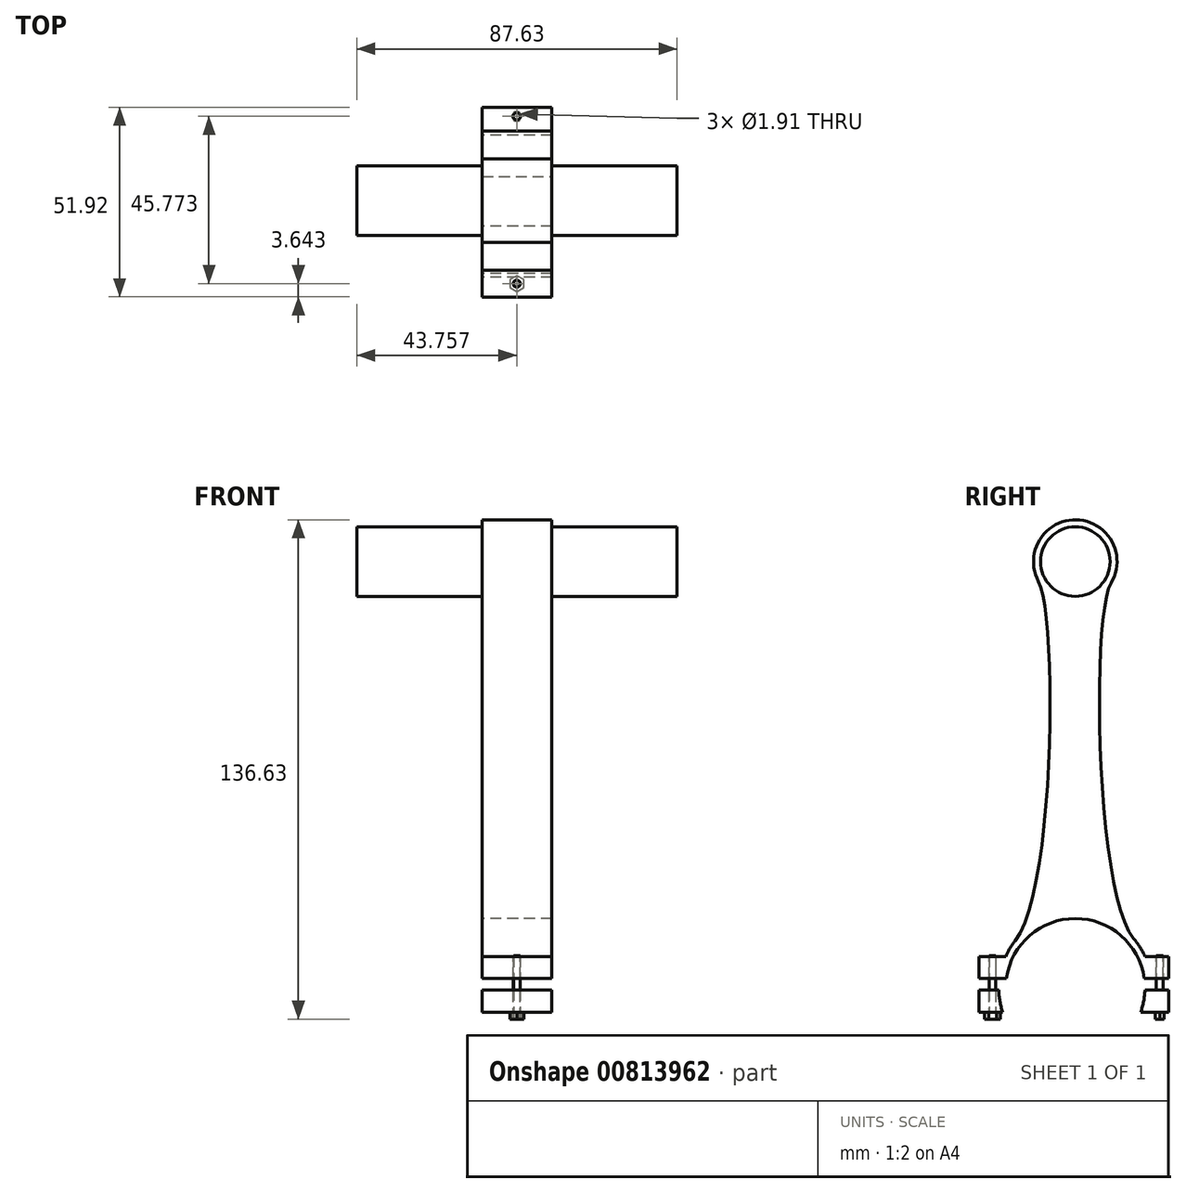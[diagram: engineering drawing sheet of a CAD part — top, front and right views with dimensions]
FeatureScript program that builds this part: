
annotation { "Feature Type Name" : "Feature", "Feature Type Description" : "" }
export const myFeature = defineFeature(function(context is Context, id is Id, definition is map)
    precondition{}
    {
        {
            var Q0;
            Q0=qCreatedBy(makeId("Right.planeOp"),FACE);
            var sketch = newSketch(context, id + "F0", { "sketchPlane" : qUnion([Q0])});
            skArc(sketch, "E0", {"start": v(-29.36, -1.03) * mm, "mid": v(-15.4, -14.68) * mm, "end": v(-1.43, -1.03) * mm});
            skCircle(sketch, "E1", {"center": v(-15.4, 77.12) * mm, "radius": 7.62 * mm});
            skFitSpline(sketch, "E2", {"points": [v(-22.11, 73.5) * mm, v(-26.4, 7.9) * mm], "startDerivative": vector(10.11, -18.68) * mm, "endDerivative": vector(-22.39, -28.64) * mm});
            skFitSpline(sketch, "E3", {"points": [v(-8.9, 73.18) * mm, v(-4.77, 8.36) * mm], "startDerivative": vector(-10.82, -17.88) * mm, "endDerivative": vector(20.78, -24.37) * mm});
            skCircle(sketch, "E4", {"center": v(-15.4, 77.12) * mm, "radius": 6.35 * mm});
            skArc(sketch, "E5", {"start": v(-28.1, -1.03) * mm, "mid": v(-15.4, -13.4) * mm, "end": v(-2.7, -1.03) * mm});
            skLineSegment(sketch, "E6", {"start": v(-29.35, 0) * mm, "end": v(-1.45, 0) * mm});
            skLineSegment(sketch, "E7.bottom", {"start": v(-32.95, 5.08) * mm, "end": v(1.67, 5.08) * mm});
            skLineSegment(sketch, "E7.top", {"start": v(-32.95, 0) * mm, "end": v(1.67, 0) * mm});
            skLineSegment(sketch, "E7.left", {"start": v(-32.95, 5.08) * mm, "end": v(-32.95, 1.1) * mm});
            skLineSegment(sketch, "E7.right", {"start": v(1.67, 5.08) * mm, "end": v(1.67, 1.1) * mm});
            skLineSegment(sketch, "E8.top", {"start": v(-29.35, 0) * mm, "end": v(1.67, 0) * mm});
            skLineSegment(sketch, "E8.left", {"start": v(-32.95, 0) * mm, "end": v(-32.95, 0) * mm});
            skLineSegment(sketch, "E8.right", {"start": v(1.67, 0) * mm, "end": v(1.67, 0) * mm});
            skLineSegment(sketch, "E9.bottom", {"start": v(-32.95, -5.08) * mm, "end": v(1.67, -5.08) * mm});
            skLineSegment(sketch, "E9.left", {"start": v(-32.95, -5.08) * mm, "end": v(-32.95, -1.03) * mm});
            skLineSegment(sketch, "E9.right", {"start": v(1.67, -5.08) * mm, "end": v(1.67, -1.03) * mm});
            skLineSegment(sketch, "E10.bottom", {"start": v(-32.95, 1.1) * mm, "end": v(1.67, 1.1) * mm});
            skLineSegment(sketch, "E10.top", {"start": v(-32.95, -1.03) * mm, "end": v(1.67, -1.03) * mm});
            skArc(sketch, "E11.trimOffspring", {"start": v(-2.83, 1.1) * mm, "mid": v(-15.4, 12) * mm, "end": v(-27.97, 1.1) * mm});
            skArc(sketch, "E12.trimOffspring", {"start": v(-1.54, 1.1) * mm, "mid": v(-15.4, 13.26) * mm, "end": v(-29.25, 1.1) * mm});
            skSolve(sketch);
        }
        {
            var Q0;
            {var subQ0=sQuery(id+"F0.wireOp",EDGE,"E2");Q0=makeQuery(id+"F0.imprint","IMPRINT",FACE,{"disambiguationData":[TD([[makeQuery(id+"F0.imprint","IMPRINT",EDGE,{"derivedFrom":subQ0}),1.0]])]});}
            var Q1;
            {var subQ1=sQuery(id+"F0.wireOp",EDGE,"E7.bottom");var subQ4=sQuery(id+"F0.wireOp",EDGE,"E12.trimOffspring");var subQ7=makeQuery(id+"F0.imprint","INTERSECT",VERTEX,{"disambiguationData":[OD(0.0)],"derivedFrom":[subQ1,subQ4]});Q1=makeQuery(id+"F0.imprint","IMPRINT",FACE,{"disambiguationData":[TD([[makeQuery(id+"F0.imprint","IMPRINT",EDGE,{"disambiguationData":[TD([[subQ7,-1.0]])],"derivedFrom":subQ1}),1.0]])]});}
            var Q2;
            {var subQ0=sQuery(id+"F0.wireOp",EDGE,"E7.left");Q2=makeQuery(id+"F0.imprint","IMPRINT",FACE,{"disambiguationData":[TD([[makeQuery(id+"F0.imprint","IMPRINT",EDGE,{"derivedFrom":subQ0}),1.0]])]});}
            var Q3;
            {var subQ0=sQuery(id+"F0.wireOp",EDGE,"E12.trimOffspring");var subQ1=sQuery(id+"F0.wireOp",EDGE,"E7.bottom");var subQ2=makeQuery(id+"F0.imprint","INTERSECT",VERTEX,{"disambiguationData":[OD(0.0)],"derivedFrom":[subQ1,subQ0]});Q3=makeQuery(id+"F0.imprint","IMPRINT",FACE,{"disambiguationData":[TD([[makeQuery(id+"F0.imprint","IMPRINT",EDGE,{"disambiguationData":[TD([[subQ2,-1.0]])],"derivedFrom":subQ1}),-1.0]])]});}
            var Q4;
            {var subQ0=sQuery(id+"F0.wireOp",EDGE,"E12.trimOffspring");var subQ1=sQuery(id+"F0.wireOp",EDGE,"E7.bottom");var subQ2=makeQuery(id+"F0.imprint","INTERSECT",VERTEX,{"disambiguationData":[OD(1.0)],"derivedFrom":[subQ1,subQ0]});Q4=makeQuery(id+"F0.imprint","IMPRINT",FACE,{"disambiguationData":[TD([[makeQuery(id+"F0.imprint","IMPRINT",EDGE,{"disambiguationData":[TD([[subQ2,1.0]])],"derivedFrom":subQ1}),-1.0]])]});}
            var Q5;
            {var subQ0=sQuery(id+"F0.wireOp",EDGE,"E7.right");Q5=makeQuery(id+"F0.imprint","IMPRINT",FACE,{"disambiguationData":[TD([[makeQuery(id+"F0.imprint","IMPRINT",EDGE,{"derivedFrom":subQ0}),-1.0]])]});}
            var Q6;
            {var subQ5=sQuery(id+"F0.wireOp",EDGE,"E9.right");Q6=makeQuery(id+"F0.imprint","IMPRINT",FACE,{"disambiguationData":[TD([[makeQuery(id+"F0.imprint","IMPRINT",EDGE,{"derivedFrom":subQ5}),1.0]])]});}
            var Q7;
            {var subQ0=sQuery(id+"F0.wireOp",EDGE,"E10.top");var subQ1=sQuery(id+"F0.wireOp",EDGE,"E0");var subQ2=makeQuery(id+"F0.imprint","INTERSECT",VERTEX,{"disambiguationData":[OD(1.0)],"derivedFrom":[subQ1,subQ0]});Q7=makeQuery(id+"F0.imprint","IMPRINT",FACE,{"disambiguationData":[TD([[makeQuery(id+"F0.imprint","IMPRINT",EDGE,{"disambiguationData":[TD([[subQ2,1.0]])],"derivedFrom":subQ1}),1.0]])]});}
            var Q8;
            {var subQ0=sQuery(id+"F0.wireOp",EDGE,"E9.bottom");var subQ1=sQuery(id+"F0.wireOp",EDGE,"E0");var subQ2=makeQuery(id+"F0.imprint","INTERSECT",VERTEX,{"disambiguationData":[OD(0.0)],"derivedFrom":[subQ1,subQ0]});Q8=makeQuery(id+"F0.imprint","IMPRINT",FACE,{"disambiguationData":[TD([[makeQuery(id+"F0.imprint","IMPRINT",EDGE,{"disambiguationData":[TD([[subQ2,-1.0]])],"derivedFrom":subQ1}),1.0]])]});}
            var Q9;
            {var subQ0=sQuery(id+"F0.wireOp",EDGE,"E10.top");var subQ1=sQuery(id+"F0.wireOp",EDGE,"E0");var subQ2=makeQuery(id+"F0.imprint","INTERSECT",VERTEX,{"disambiguationData":[OD(0.0)],"derivedFrom":[subQ1,subQ0]});Q9=makeQuery(id+"F0.imprint","IMPRINT",FACE,{"disambiguationData":[TD([[makeQuery(id+"F0.imprint","IMPRINT",EDGE,{"disambiguationData":[TD([[subQ2,-1.0]])],"derivedFrom":subQ1}),1.0]])]});}
            var Q10;
            {var subQ5=sQuery(id+"F0.wireOp",EDGE,"E9.left");Q10=makeQuery(id+"F0.imprint","IMPRINT",FACE,{"disambiguationData":[TD([[makeQuery(id+"F0.imprint","IMPRINT",EDGE,{"derivedFrom":subQ5}),-1.0]])]});}
            var Q11;
            Q11=makeQuery(id+"F0.imprint","IMPRINT",FACE,{"disambiguationData":[TD([[makeQuery(id+"F0.imprint","IMPRINT",EDGE,{"derivedFrom":sQuery(id+"F0.wireOp",EDGE,"E4")}),-1.0]])]});
            extrude(context, id + "F1", {"entities" : qUnion([Q0, Q1, Q2, Q3, Q4, Q5, Q6, Q7, Q8, Q9, Q10, Q11]), "depth" : 12.7 * mm, "offsetDistance" : 25.4 * mm});
        }
        {
            var Q0;
            {var subQ0=sQuery(id+"F0.wireOp",EDGE,"E7.bottom");Q0=makeQuery(id+"F1.opExtrude","SWEPT_FACE",FACE,{"disambiguationData":[OSD([subQ0]),TDD([makeQuery(id+"F0.imprint","IMPRINT",EDGE,{"disambiguationData":[TD([[makeQuery(id+"F0.imprint","INTERSECT",VERTEX,{"derivedFrom":[subQ0,sQuery(id+"F0.wireOp",EDGE,"E7.right")]}),1.0]])],"derivedFrom":subQ0})])]});}
            var sketch = newSketch(context, id + "F2", { "sketchPlane" : qUnion([Q0])});
            skCircle(sketch, "E13", {"center": v(6.31, 0) * mm, "radius": 0.64 * mm});
            skCircle(sketch, "E14", {"center": v(6.31, -30.52) * mm, "radius": 0.64 * mm});
            skSolve(sketch);
        }
        {
            var Q0;
            Q0=makeQuery(id+"F2.imprint","IMPRINT",FACE,{"disambiguationData":[TD([[makeQuery(id+"F2.imprint","IMPRINT",EDGE,{"derivedFrom":sQuery(id+"F2.wireOp",EDGE,"E14")}),1.0]])]});
            var Q1;
            Q1=makeQuery(id+"F2.imprint","IMPRINT",FACE,{"disambiguationData":[TD([[makeQuery(id+"F2.imprint","IMPRINT",EDGE,{"derivedFrom":sQuery(id+"F2.wireOp",EDGE,"E13")}),1.0]])]});
            extrude(context, id + "F3", {"entities" : qUnion([Q0, Q1]), "operationType" : NewBodyOperationType.REMOVE, "oppositeDirection" : true, "depth" : 25.4 * mm, "offsetDistance" : 25.4 * mm});
        }
        {
            var Q0;
            {var subQ0=sQuery(id+"F0.wireOp",EDGE,"E9.bottom");Q0=makeQuery(id+"F1.opExtrude","SWEPT_FACE",FACE,{"disambiguationData":[OSD([subQ0]),TDD([makeQuery(id+"F0.imprint","IMPRINT",EDGE,{"disambiguationData":[TD([[makeQuery(id+"F0.imprint","INTERSECT",VERTEX,{"derivedFrom":[subQ0,sQuery(id+"F0.wireOp",EDGE,"E9.left")]}),-1.0]])],"derivedFrom":subQ0})])]});}
            var sketch = newSketch(context, id + "F4", { "sketchPlane" : qUnion([Q0])});
            skCircle(sketch, "E15", {"center": v(6.31, 30.52) * mm, "radius": 0.6 * mm});
            skCircle(sketch, "E16.cCircle", {"center": v(6.31, 30.52) * mm, "radius": 1.26 * mm, "construction": true});
            skLineSegment(sketch, "E16.0", {"start": v(5.05, 29.79) * mm, "end": v(5.05, 31.24) * mm});
            skLineSegment(sketch, "E16.1", {"start": v(5.05, 31.24) * mm, "end": v(6.31, 31.97) * mm});
            skLineSegment(sketch, "E16.2", {"start": v(6.31, 31.97) * mm, "end": v(7.58, 31.24) * mm});
            skLineSegment(sketch, "E16.3", {"start": v(7.58, 31.24) * mm, "end": v(7.58, 29.79) * mm});
            skLineSegment(sketch, "E16.4", {"start": v(7.58, 29.79) * mm, "end": v(6.31, 29.06) * mm});
            skLineSegment(sketch, "E16.5", {"start": v(6.31, 29.06) * mm, "end": v(5.05, 29.79) * mm});
            skPoint(sketch, "E16.0.midPoint", {"position": v(5.05, 30.52) * mm});
            skCircle(sketch, "E17", {"center": v(6.3, 0) * mm, "radius": 0.64 * mm});
            skCircle(sketch, "E18.cCircle", {"center": v(6.3, 0) * mm, "radius": 0.83 * mm, "construction": true});
            skLineSegment(sketch, "E18.0", {"start": v(5.83, 0.83) * mm, "end": v(6.79, 0.83) * mm});
            skLineSegment(sketch, "E18.1", {"start": v(6.79, 0.83) * mm, "end": v(7.26, 0) * mm});
            skLineSegment(sketch, "E18.2", {"start": v(7.26, 0) * mm, "end": v(6.79, -0.83) * mm});
            skLineSegment(sketch, "E18.3", {"start": v(6.79, -0.83) * mm, "end": v(5.83, -0.83) * mm});
            skLineSegment(sketch, "E18.4", {"start": v(5.83, -0.83) * mm, "end": v(5.36, 0) * mm});
            skLineSegment(sketch, "E18.5", {"start": v(5.36, 0) * mm, "end": v(5.83, 0.83) * mm});
            skPoint(sketch, "E18.0.midPoint", {"position": v(6.3, 0.83) * mm});
            skSolve(sketch);
        }
        {
            var Q0;
            Q0=makeQuery(id+"F4.imprint","IMPRINT",FACE,{"disambiguationData":[TD([[makeQuery(id+"F4.imprint","IMPRINT",EDGE,{"derivedFrom":sQuery(id+"F4.wireOp",EDGE,"E17")}),1.0]])]});
            var Q1;
            Q1=makeQuery(id+"F4.imprint","IMPRINT",FACE,{"disambiguationData":[TD([[makeQuery(id+"F4.imprint","IMPRINT",EDGE,{"derivedFrom":sQuery(id+"F4.wireOp",EDGE,"E15")}),1.0]])]});
            extrude(context, id + "F5", {"entities" : qUnion([Q0, Q1]), "oppositeDirection" : true, "depth" : 10.29 * mm, "offsetDistance" : 25.4 * mm, "hasSecondDirection" : true, "secondDirectionOppositeDirection" : false, "secondDirectionDepth" : 1.27 * mm});
        }
        {
            var Q0;
            Q0=makeQuery(id+"F4.imprint","IMPRINT",FACE,{"disambiguationData":[TD([[makeQuery(id+"F4.imprint","IMPRINT",EDGE,{"derivedFrom":sQuery(id+"F4.wireOp",EDGE,"E17")}),-1.0]])]});
            var Q1;
            Q1=makeQuery(id+"F4.imprint","IMPRINT",FACE,{"disambiguationData":[TD([[makeQuery(id+"F4.imprint","IMPRINT",EDGE,{"derivedFrom":sQuery(id+"F4.wireOp",EDGE,"E16.0")}),-1.0]])]});
            extrude(context, id + "F6", {"entities" : qUnion([Q0, Q1]), "operationType" : NewBodyOperationType.ADD, "depth" : 1.27 * mm, "offsetDistance" : 25.4 * mm});
        }
        {
            var Q0;
            Q0=makeQuery(id+"F0.imprint","IMPRINT",FACE,{"disambiguationData":[TD([[makeQuery(id+"F0.imprint","IMPRINT",EDGE,{"derivedFrom":sQuery(id+"F0.wireOp",EDGE,"E4")}),1.0]])]});
            extrude(context, id + "F7", {"entities" : qUnion([Q0]), "operationType" : NewBodyOperationType.ADD, "depth" : 35.56 * mm, "offsetDistance" : 25.4 * mm, "hasSecondDirection" : true, "secondDirectionOppositeDirection" : true, "secondDirectionDepth" : 22.86 * mm});
        }
        {
            var Q0;
            Q0=makeQuery(id+"F1.opExtrude","SWEPT_BODY",BODY,{"disambiguationData":[OSD([sQuery(id+"F0.wireOp",EDGE,"E0"),sQuery(id+"F0.wireOp",EDGE,"E5"),sQuery(id+"F0.wireOp",EDGE,"E9.bottom"),sQuery(id+"F0.wireOp",EDGE,"E9.left"),sQuery(id+"F0.wireOp",EDGE,"E9.right"),sQuery(id+"F0.wireOp",EDGE,"E10.top")])]});
            var Q1;
            Q1=makeQuery(id+"F1.opExtrude","SWEPT_BODY",BODY,{"disambiguationData":[OSD([sQuery(id+"F0.wireOp",EDGE,"E1"),sQuery(id+"F0.wireOp",EDGE,"E2"),sQuery(id+"F0.wireOp",EDGE,"E3"),sQuery(id+"F0.wireOp",EDGE,"E4"),sQuery(id+"F0.wireOp",EDGE,"E7.bottom"),sQuery(id+"F0.wireOp",EDGE,"E7.left"),sQuery(id+"F0.wireOp",EDGE,"E7.right"),sQuery(id+"F0.wireOp",EDGE,"E10.bottom"),sQuery(id+"F0.wireOp",EDGE,"E11.trimOffspring"),sQuery(id+"F0.wireOp",EDGE,"E12.trimOffspring")])]});
            var Q2;
            Q2=makeQuery(id+"F5.opExtrude","SWEPT_BODY",BODY,{"disambiguationData":[OSD([sQuery(id+"F4.wireOp",EDGE,"E15")])]});
            var Q3;
            Q3=makeQuery(id+"F5.opExtrude","SWEPT_BODY",BODY,{"disambiguationData":[OSD([sQuery(id+"F4.wireOp",EDGE,"E17")])]});
            var Q4;
            Q4=sQuery(id+"F0.wireOp",VERTEX,"E3.start");
            transform(context, id + "F8", {"entities" : qUnion([Q0, Q1, Q2, Q3]), "transformType" : TransformType.SCALE_UNIFORMLY, "scale" : 1.5, "scalePoint" : qUnion([Q4]), "makeCopy" : false});
        }
    });
